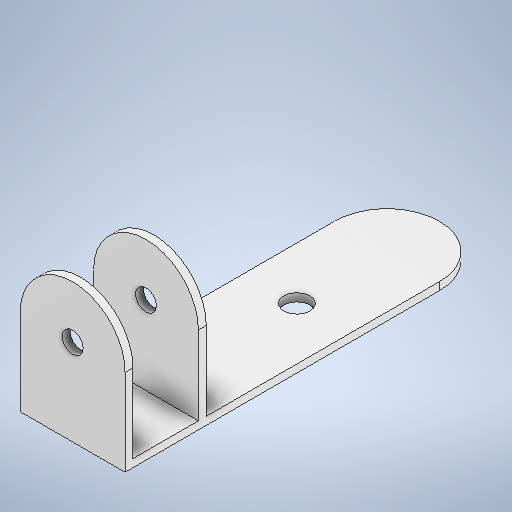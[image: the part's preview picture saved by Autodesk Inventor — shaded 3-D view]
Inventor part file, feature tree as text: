
AUTODESK INVENTOR PART (.ipt)
format: ipt  version: 2025.3 (Build 293356000, 356)  size: 268,288 bytes
history: native  units: mm
features: extrude x5, sketch x5, other x2
ambient origin geometry x8: Origin, YZ Plane, XZ Plane, XY Plane, X Axis, Y Axis, Z Axis, Center Point
bodies: Body1 (feature_tree)
feature tree (12):
  other  "Base_engine"
  other  "Sólido1"
  extrude  "Extrusión1"  Depth=80.0mm
  extrude  "Extrusión2"  Depth=3.0mm
  extrude  "Extrusión3"  Depth=3.0mm
  extrude  "Extrusión4"  Depth=3.0mm
  extrude  "Extrusión5"  Depth=40.0mm TaperAngle=0.0deg
  sketch  "Boceto1"  dims[d0=60.0mm d1=80.0mm]
  sketch  "Boceto2"  dims[d2=3.0mm d3=140.0mm]
  sketch  "Boceto3"  dims[d4=50.0mm d5=3.0mm]
  sketch  "Boceto4"  dims[d6=50.0mm d7=3.0mm]
  sketch  "Boceto5"  dims[d8=25.0mm d9=40.0mm d10=0.0mm d11=40.0mm d12=0.0mm d13=40.0mm d14=0.0mm d15=8.0mm d16=40.0mm d17=0.0mm d20=10.0mm d21=10.0mm d22=40.0mm d23=0.0mm]
